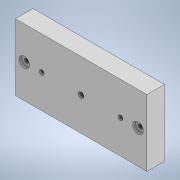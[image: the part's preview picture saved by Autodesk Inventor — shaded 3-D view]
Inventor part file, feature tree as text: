
AUTODESK INVENTOR PART (.ipt)
format: ipt  version: 2022.2 (Build 262287030, 287C)  size: 120,832 bytes
history: native  units: in
note: dims shown in document units (in); Inventor stores cm internally (conversion verified against a paired STEP export)
features: sketch x4, hole x3, extrude x1, projected_geometry x1
ambient origin geometry x8: Origin, YZ Plane, XZ Plane, XY Plane, X Axis, Y Axis, Z Axis, Center Point
bodies: Solid1 (feature_tree)
feature tree (9):
  extrude  "Extrusion1"  Depth=1.4961in
  hole  "Hole2"  [1 undecoded]
  hole  "Hole3"  [1 undecoded]
  hole  "Hole4"  [1 undecoded]
  sketch  "Sketch1"  dims[d0=0.3937in d1=0.0in d2=1.4961in]
  sketch  "Sketch3"  dims[d3=2.9528in]
  sketch  "Sketch4"  dims[d69=0.125in d70=0.2953in d71=0.1476in d72=0.0984in d73=90.0deg d74=0.1969in d75=0.8108in d76=0.1969in]
  projected_geometry  "Projected Loop2"
  sketch  "Sketch5"  dims[d77=0.7874in d79=2.5591in d80=0.3937in d82=0.3937in d84=0.0968in d85=0.2362in d86=0.2362in d87=0.0551in d88=90.0deg d89=0.1969in d90=0.8108in d95=0.8858in d96=0.8858in d97=0.1063in d98=0.2953in d99=0.1476in d100=0.0984in d101=90.0deg d102=0.1181in d103=0.8108in d62=0.3937in d63=0.3937in d64=0.3937in d65=0.0591in d66=0.0984in d67=0.1476in d68=0.5635in]
note: 3 required parameter values undecoded (feature->parameter linkage not recoverable at this tier; creation-order binding heuristic only, values carry confidence <= 0.55)
